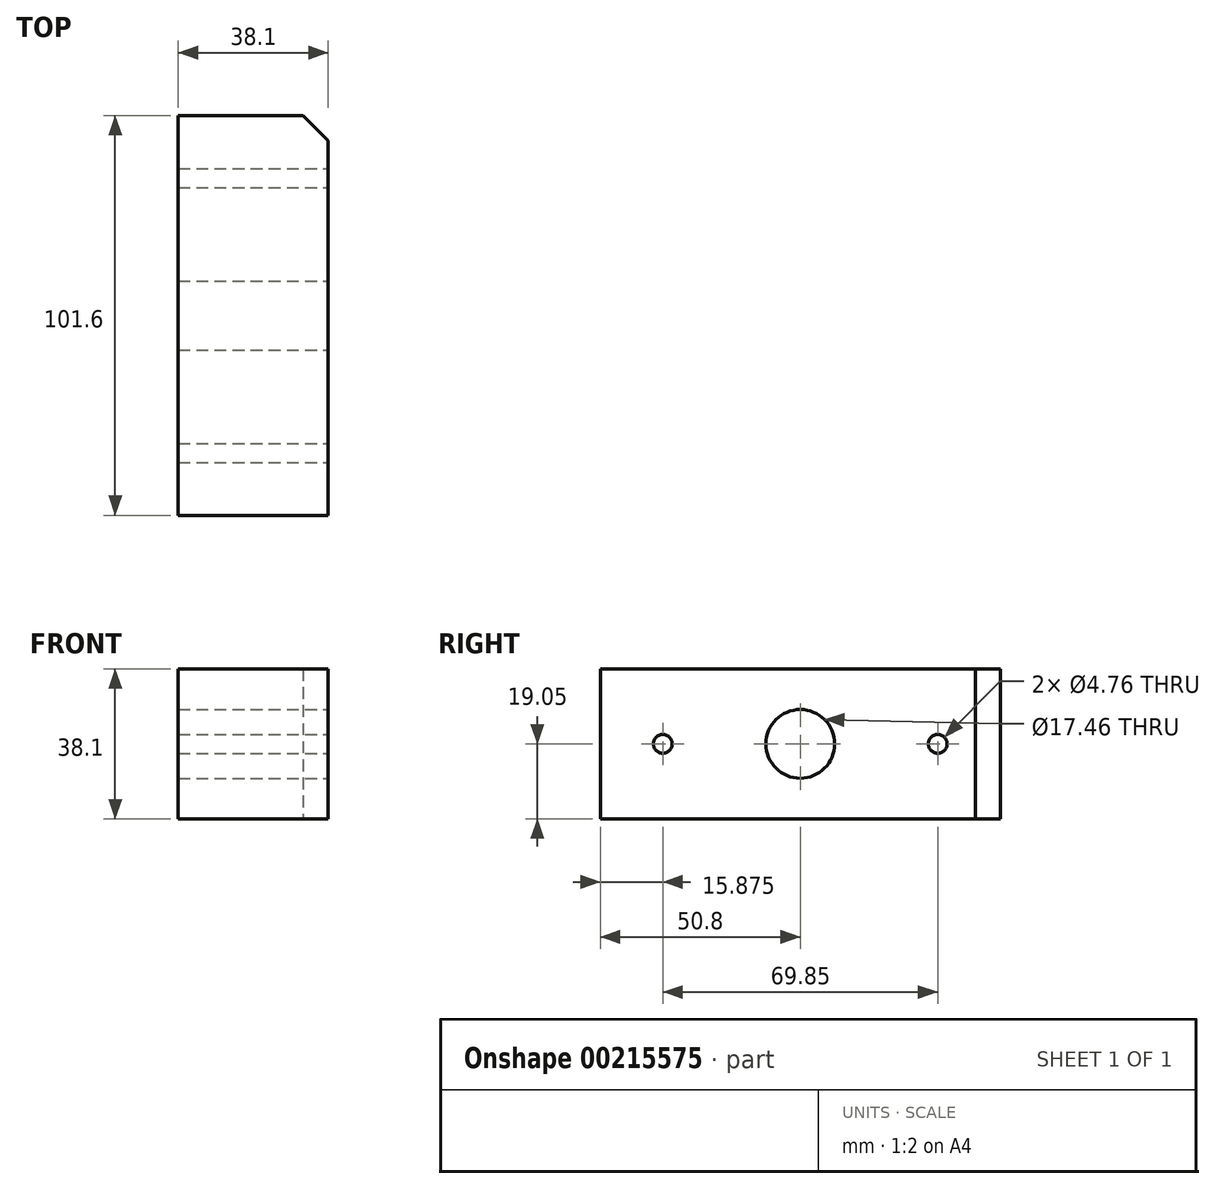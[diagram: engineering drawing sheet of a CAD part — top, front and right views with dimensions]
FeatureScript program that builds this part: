
annotation { "Feature Type Name" : "Feature", "Feature Type Description" : "" }
export const myFeature = defineFeature(function(context is Context, id is Id, definition is map)
    precondition{}
    {
        {
            var Q0;
            Q0=qCreatedBy(makeId("Front.planeOp"),FACE);
            var sketch = newSketch(context, id + "F0", { "sketchPlane" : qUnion([Q0])});
            skLineSegment(sketch, "E0.bottom", {"start": v(19.05, 19.05) * mm, "end": v(-19.05, 19.05) * mm});
            skLineSegment(sketch, "E0.top", {"start": v(19.05, -19.05) * mm, "end": v(-19.05, -19.05) * mm});
            skLineSegment(sketch, "E0.left", {"start": v(19.05, 19.05) * mm, "end": v(19.05, -19.05) * mm});
            skLineSegment(sketch, "E0.right", {"start": v(-19.05, 19.05) * mm, "end": v(-19.05, -19.05) * mm});
            skPoint(sketch, "E0.middle", {"position": v(0, 0) * mm});
            skSolve(sketch);
        }
        {
            var Q0;
            Q0=makeQuery(id+"F0.imprint","IMPRINT",FACE,{"disambiguationData":[TD([[makeQuery(id+"F0.imprint","IMPRINT",EDGE,{"derivedFrom":sQuery(id+"F0.wireOp",EDGE,"E0.bottom")}),1.0]])]});
            extrude(context, id + "F1", {"entities" : qUnion([Q0]), "oppositeDirection" : true, "depth" : 101.6 * mm});
        }
        {
            var Q0;
            Q0=makeQuery(id+"F1.opExtrude","CAP_EDGE",EDGE,{"disambiguationData":[OSD([sQuery(id+"F0.wireOp",EDGE,"E0.left")])],"isStart":false});
            chamfer(context, id + "F2", {"entities" : qUnion([Q0]), "width" : 6.35 * mm, "tangentPropagation" : true});
        }
        {
            var Q0;
            Q0=makeQuery(id+"F1.opExtrude","SWEPT_FACE",FACE,{"disambiguationData":[OSD([sQuery(id+"F0.wireOp",EDGE,"E0.left")])]});
            var sketch = newSketch(context, id + "F3", { "sketchPlane" : qUnion([Q0])});
            skLineSegment(sketch, "E1", {"start": v(0, 0) * mm, "end": v(118.65, 0) * mm, "construction": true});
            skPoint(sketch, "E2.endSnap0", {"position": v(47.63, -19.05) * mm});
            skLineSegment(sketch, "E3", {"start": v(15.88, 39.37) * mm, "end": v(15.88, -44.83) * mm, "construction": true});
            skLineSegment(sketch, "E4", {"start": v(85.73, 37.44) * mm, "end": v(85.73, -31.98) * mm, "construction": true});
            skLineSegment(sketch, "E5", {"start": v(50.8, 38.18) * mm, "end": v(50.8, -43.12) * mm, "construction": true});
            skPoint(sketch, "E6", {"position": v(50.8, 0) * mm});
            skPoint(sketch, "E7", {"position": v(15.88, 0) * mm});
            skPoint(sketch, "E8", {"position": v(85.73, 0) * mm});
            skSolve(sketch);
        }
        {
            var Q0;
            Q0=sQuery(id+"F3.wireOp",VERTEX,"E6");
            var Q1;
            Q1=makeQuery(id+"F1.opExtrude","SWEPT_BODY",BODY,{"disambiguationData":[OSD([sQuery(id+"F0.wireOp",EDGE,"E0.bottom"),sQuery(id+"F0.wireOp",EDGE,"E0.top"),sQuery(id+"F0.wireOp",EDGE,"E0.left"),sQuery(id+"F0.wireOp",EDGE,"E0.right")])]});
            hole(context, id + "F4", {"style" : HoleStyle.SIMPLE, "endStyle" : HoleEndStyle.THROUGH, "holeDiameter" : 17.46 * mm, "locations" : qUnion([Q0]), "scope" : qUnion([Q1]), "isTappedThrough" : true});
        }
        {
            var Q0;
            Q0=sQuery(id+"F3.wireOp",VERTEX,"E7");
            var Q1;
            Q1=sQuery(id+"F3.wireOp",VERTEX,"E8");
            var Q2;
            Q2=makeQuery(id+"F1.opExtrude","SWEPT_BODY",BODY,{"disambiguationData":[OSD([sQuery(id+"F0.wireOp",EDGE,"E0.bottom"),sQuery(id+"F0.wireOp",EDGE,"E0.top"),sQuery(id+"F0.wireOp",EDGE,"E0.left"),sQuery(id+"F0.wireOp",EDGE,"E0.right")])]});
            hole(context, id + "F5", {"style" : HoleStyle.SIMPLE, "endStyle" : HoleEndStyle.THROUGH, "holeDiameter" : 4.76 * mm, "locations" : qUnion([Q0, Q1]), "scope" : qUnion([Q2]), "isTappedThrough" : true});
        }
    });
